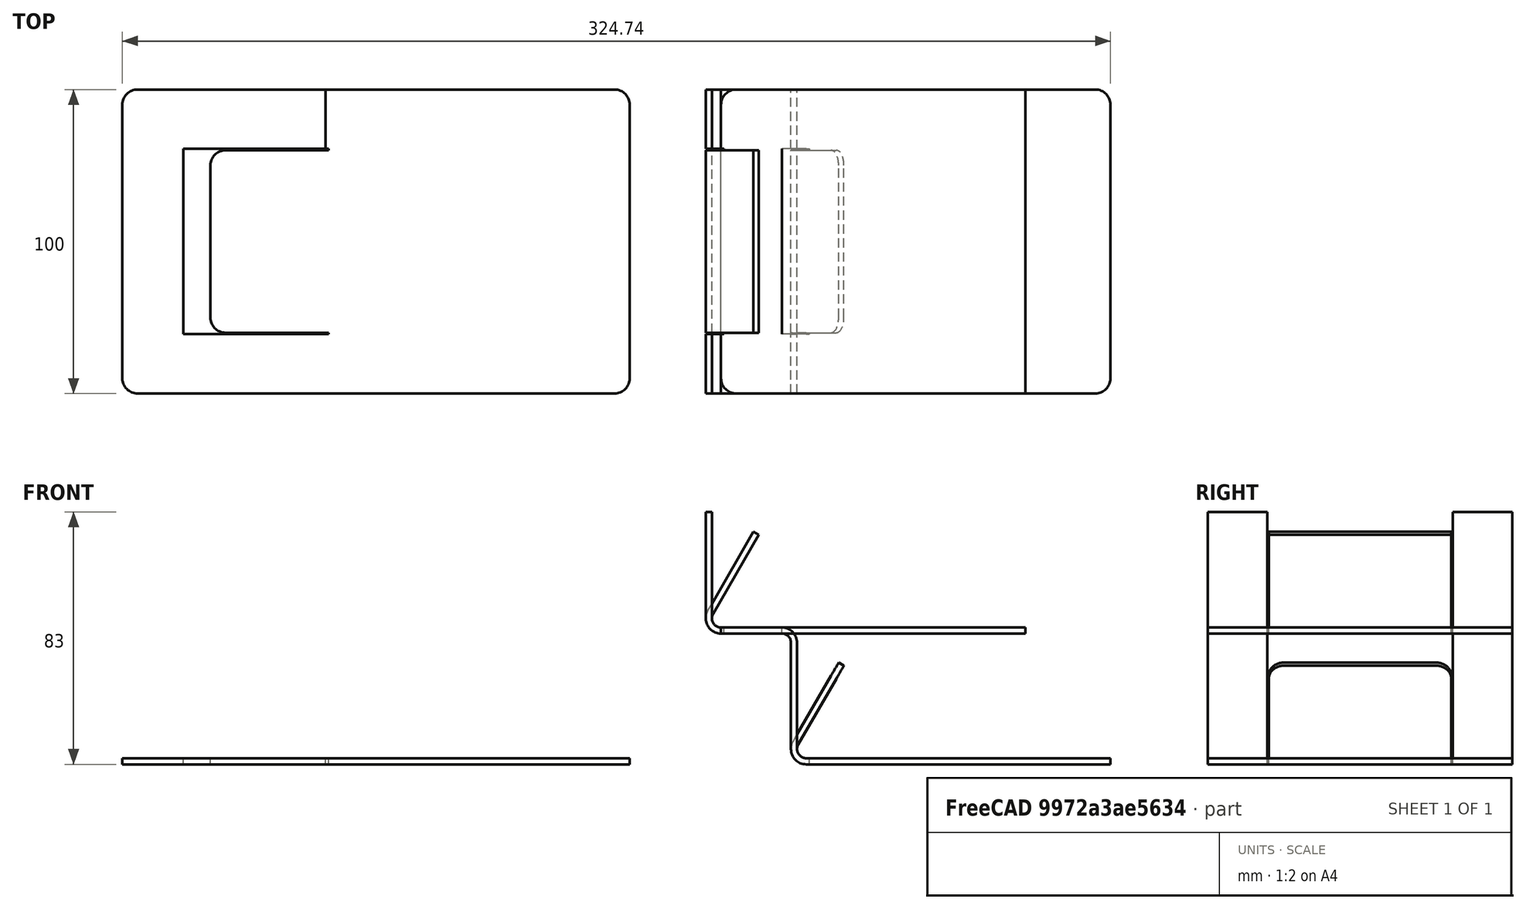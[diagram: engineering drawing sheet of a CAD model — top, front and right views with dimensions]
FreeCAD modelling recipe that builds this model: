
FCSTD DOCUMENT  (FreeCAD 0.17R13452 (Git))
Label: bend
License: All rights reserved
LicenseURL: http://en.wikipedia.org/wiki/All_rights_reserved
objects: Part::FeaturePython×3, Part::Box×2, Part::MultiFuse×1, Part::Fillet×1, Part::Feature×1
note: 8 computed .brp shape members not serialized (recipe doc carries the construction recipe); baked Part::Feature solids carry a one-line shape summary decoded from their .brp

FEATURE [Part::Box] Box  label="Cube"
  AttacherType = Attacher::AttachEngine3D
  Height = 2
  Length = 100
  Width = 100
FEATURE [Part::FeaturePython] Bend  # WARN: FeaturePython — macro-defined, semantics opaque (R4)
  angle = 120
  baseObject = -> Box [Face1]
  gap1 = 20
  gap2 = 20
  invert = false
  length = 30
  miterangle1 = 0
  miterangle2 = 0
  radius = 3
  reliefd = 1
  reliefw = 0.5
FEATURE [Part::FeaturePython] Bend001  # WARN: FeaturePython — macro-defined, semantics opaque (R4)
  angle = 90
  baseObject = -> Bend [Face15,Face20]
  gap1 = 0
  gap2 = 0
  invert = false
  length = 35
  miterangle1 = 0
  miterangle2 = 0
  radius = 3
  reliefd = 1
  reliefw = 0.5
FEATURE [Part::FeaturePython] Bend002  # WARN: FeaturePython — macro-defined, semantics opaque (R4)
  Placement = pos=(28,-2.1e-11,-43) rot=(0,0,1;0rad)
  angle = 90
  baseObject = -> Bend001 [Face34,Face1]
  gap1 = 0
  gap2 = 0
  invert = true
  length = 0
  miterangle1 = 0
  miterangle2 = 0
  radius = 3
  reliefd = 1
  reliefw = 0.5
FEATURE [Part::Box] Box001  label="Cube001"
  AttacherType = Attacher::AttachEngine3D
  Height = 2
  Length = 20
  Width = 100
FEATURE [Part::MultiFuse] Fusion
  Shapes = -> [Bend002,Box001]
FEATURE [Part::Fillet] Fillet
  Base = -> Fusion
  Edges = 6 edges r=5: [Edge1,Edge3,Edge66,Edge80,Edge109,Edge110]
FEATURE [Part::Feature] Unfold
  Placement = pos=(-158,0,0) rot=(0,0,1;0rad)
  shape: bbox 166.7 x 100 x 2 mm, 58 faces (baked)
